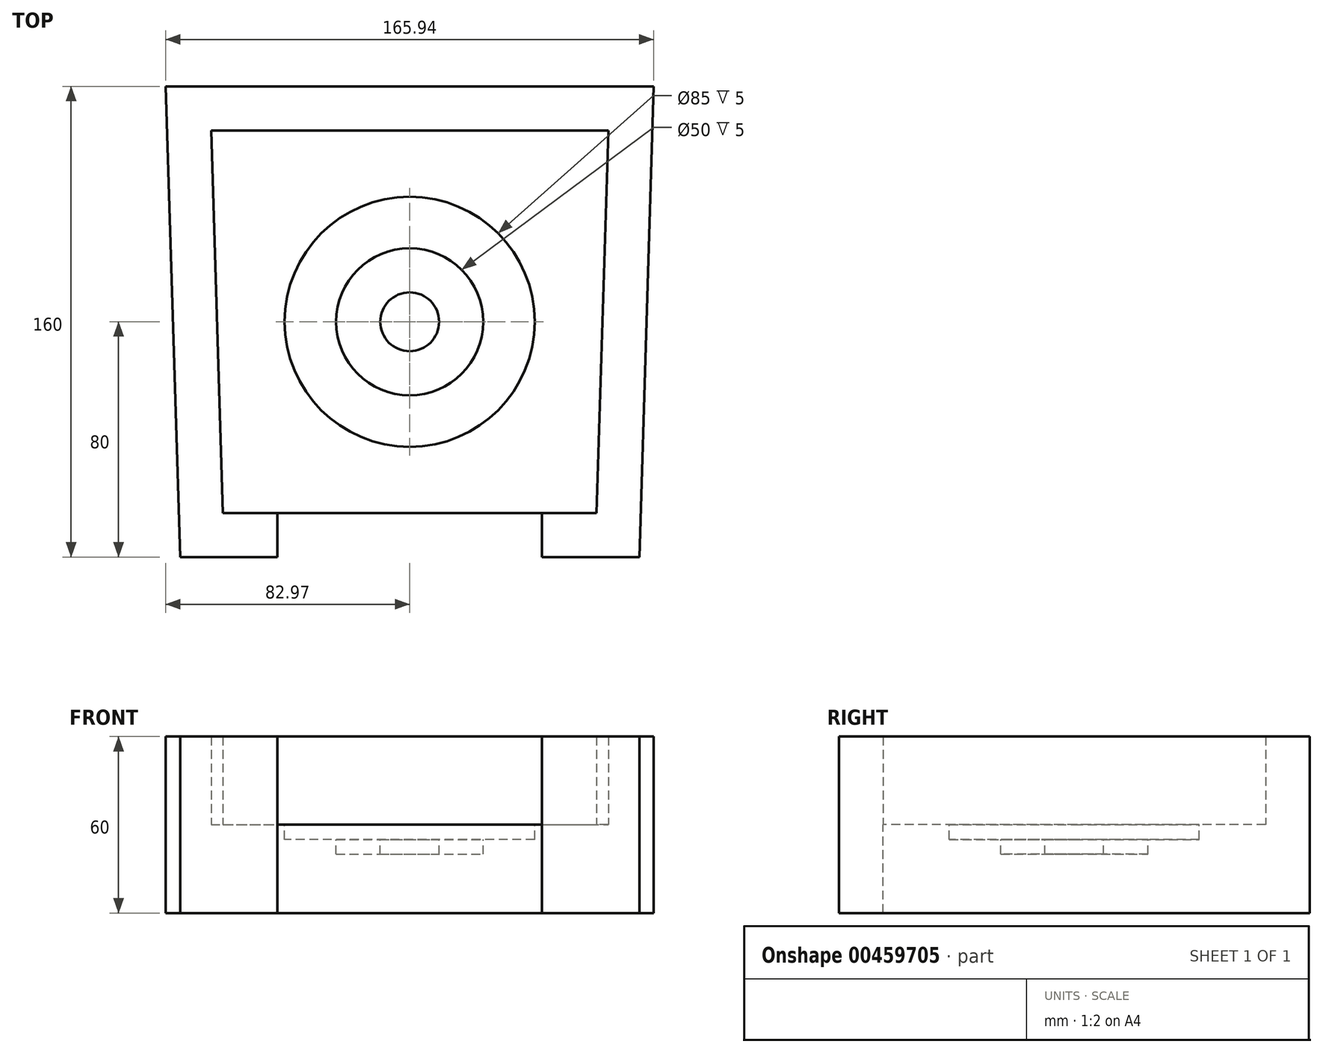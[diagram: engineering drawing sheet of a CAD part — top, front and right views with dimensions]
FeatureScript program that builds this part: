
annotation { "Feature Type Name" : "Feature", "Feature Type Description" : "" }
export const myFeature = defineFeature(function(context is Context, id is Id, definition is map)
    precondition{}
    {
        {
            var Q0;
            Q0=qCreatedBy(makeId("Top.planeOp"),FACE);
            var sketch = newSketch(context, id + "F0", { "sketchPlane" : qUnion([Q0])});
            skLineSegment(sketch, "E0", {"start": v(-67.5, 65) * mm, "end": v(-63.5, -65) * mm});
            skLineSegment(sketch, "E1", {"start": v(-63.5, -65) * mm, "end": v(63.5, -65) * mm});
            skLineSegment(sketch, "E2", {"start": v(-67.5, 65) * mm, "end": v(67.5, 65) * mm});
            skLineSegment(sketch, "E3", {"start": v(67.5, 65) * mm, "end": v(63.5, -65) * mm});
            skLineSegment(sketch, "E4", {"start": v(-82.97, 80) * mm, "end": v(-78.05, -80) * mm});
            skLineSegment(sketch, "E5", {"start": v(-78.05, -80) * mm, "end": v(78.05, -80) * mm});
            skLineSegment(sketch, "E6", {"start": v(-82.97, 80) * mm, "end": v(82.97, 80) * mm});
            skLineSegment(sketch, "E7", {"start": v(82.97, 80) * mm, "end": v(78.05, -80) * mm});
            skSolve(sketch);
        }
        {
            var Q0;
            Q0 = qSketchRegion(id + "F0", true);
            extrude(context, id + "F1", {"entities" : qUnion([Q0]), "depth" : 30 * mm});
        }
        {
            var Q0;
            Q0=makeQuery(id+"F1.opExtrude","SWEPT_FACE",FACE,{"disambiguationData":[OSD([sQuery(id+"F0.wireOp",EDGE,"E5")])]});
            var sketch = newSketch(context, id + "F2", { "sketchPlane" : qUnion([Q0])});
            skLineSegment(sketch, "E8.bottom", {"start": v(-45, 30) * mm, "end": v(45, 30) * mm});
            skLineSegment(sketch, "E8.top", {"start": v(-45, 0) * mm, "end": v(45, 0) * mm});
            skLineSegment(sketch, "E8.left", {"start": v(-45, 30) * mm, "end": v(-45, 0) * mm});
            skLineSegment(sketch, "E8.right", {"start": v(45, 30) * mm, "end": v(45, 0) * mm});
            skSolve(sketch);
        }
        {
            var Q0;
            Q0 = qSketchRegion(id + "F2", true);
            extrude(context, id + "F3", {"entities" : qUnion([Q0]), "operationType" : NewBodyOperationType.REMOVE, "endBound" : BoundingType.UP_TO_NEXT, "oppositeDirection" : true, "depth" : 35 * mm});
        }
        {
            var Q0;
            Q0=qCreatedBy(makeId("Top.planeOp"),FACE);
            var sketch = newSketch(context, id + "F4", { "sketchPlane" : qUnion([Q0])});
            skCircle(sketch, "E9", {"center": v(0, 0) * mm, "radius": 42.5 * mm});
            skLineSegment(sketch, "E10.bottom", {"start": v(-82.97, 80) * mm, "end": v(82.97, 80) * mm});
            skLineSegment(sketch, "E10.top", {"start": v(-45, -65) * mm, "end": v(45, -65) * mm});
            skLineSegment(sketch, "E11", {"start": v(45, -65) * mm, "end": v(45, -80) * mm});
            skLineSegment(sketch, "E12", {"start": v(-45, -65) * mm, "end": v(-45, -80) * mm});
            skLineSegment(sketch, "E13", {"start": v(-45, -80) * mm, "end": v(-78.05, -80) * mm});
            skLineSegment(sketch, "E14", {"start": v(-78.05, -80) * mm, "end": v(-82.97, 80) * mm});
            skLineSegment(sketch, "E15", {"start": v(45, -80) * mm, "end": v(78.05, -80) * mm});
            skLineSegment(sketch, "E16", {"start": v(78.05, -80) * mm, "end": v(82.97, 80) * mm});
            skSolve(sketch);
        }
        {
            var Q0;
            Q0 = qSketchRegion(id + "F4", true);
            extrude(context, id + "F5", {"entities" : qUnion([Q0]), "operationType" : NewBodyOperationType.ADD, "oppositeDirection" : true, "depth" : 5 * mm});
        }
        {
            var Q0;
            Q0=makeQuery(id+"F5.opExtrude","CAP_FACE",FACE,{"disambiguationData":[OSD([sQuery(id+"F4.wireOp",EDGE,"E9"),sQuery(id+"F4.wireOp",EDGE,"E10.bottom"),sQuery(id+"F4.wireOp",EDGE,"E10.top"),sQuery(id+"F4.wireOp",EDGE,"E11"),sQuery(id+"F4.wireOp",EDGE,"E12"),sQuery(id+"F4.wireOp",EDGE,"E13"),sQuery(id+"F4.wireOp",EDGE,"E14"),sQuery(id+"F4.wireOp",EDGE,"E15"),sQuery(id+"F4.wireOp",EDGE,"E16")])],"isStart":false});
            var sketch = newSketch(context, id + "F6", { "sketchPlane" : qUnion([Q0])});
            skCircle(sketch, "E17", {"center": v(0, 0) * mm, "radius": 10 * mm});
            skSolve(sketch);
        }
        {
            var Q0;
            Q0 = qSketchRegion(id + "F6", true);
            extrude(context, id + "F7", {"entities" : qUnion([Q0]), "depth" : 5 * mm});
        }
        {
            var Q0;
            Q0=makeQuery(id+"F5.opExtrude","CAP_FACE",FACE,{"disambiguationData":[OSD([sQuery(id+"F4.wireOp",EDGE,"E9"),sQuery(id+"F4.wireOp",EDGE,"E10.bottom"),sQuery(id+"F4.wireOp",EDGE,"E10.top"),sQuery(id+"F4.wireOp",EDGE,"E11"),sQuery(id+"F4.wireOp",EDGE,"E12"),sQuery(id+"F4.wireOp",EDGE,"E13"),sQuery(id+"F4.wireOp",EDGE,"E14"),sQuery(id+"F4.wireOp",EDGE,"E15"),sQuery(id+"F4.wireOp",EDGE,"E16")])],"isStart":false});
            var sketch = newSketch(context, id + "F8", { "sketchPlane" : qUnion([Q0])});
            skCircle(sketch, "E18", {"center": v(0, 0) * mm, "radius": 25 * mm});
            skLineSegment(sketch, "E19", {"start": v(-78.05, 80) * mm, "end": v(-82.97, -80) * mm});
            skLineSegment(sketch, "E20", {"start": v(-82.97, -80) * mm, "end": v(82.97, -80) * mm});
            skLineSegment(sketch, "E21", {"start": v(82.97, -80) * mm, "end": v(78.05, 80) * mm});
            skLineSegment(sketch, "E22", {"start": v(78.05, 80) * mm, "end": v(45, 80) * mm});
            skLineSegment(sketch, "E23", {"start": v(45, 80) * mm, "end": v(45, 65) * mm});
            skLineSegment(sketch, "E24", {"start": v(45, 65) * mm, "end": v(-45, 65) * mm});
            skLineSegment(sketch, "E25", {"start": v(-45, 65) * mm, "end": v(-45, 80) * mm});
            skLineSegment(sketch, "E26", {"start": v(-45, 80) * mm, "end": v(-78.05, 80) * mm});
            skSolve(sketch);
        }
        {
            var Q0;
            Q0 = qSketchRegion(id + "F8", true);
            extrude(context, id + "F9", {"entities" : qUnion([Q0]), "operationType" : NewBodyOperationType.ADD, "depth" : 5 * mm});
        }
        {
            var Q0;
            Q0=makeQuery(id+"F9.opExtrude","CAP_FACE",FACE,{"disambiguationData":[OSD([sQuery(id+"F8.wireOp",EDGE,"E18"),sQuery(id+"F8.wireOp",EDGE,"E19"),sQuery(id+"F8.wireOp",EDGE,"E20"),sQuery(id+"F8.wireOp",EDGE,"E21"),sQuery(id+"F8.wireOp",EDGE,"E22"),sQuery(id+"F8.wireOp",EDGE,"E23"),sQuery(id+"F8.wireOp",EDGE,"E24"),sQuery(id+"F8.wireOp",EDGE,"E25"),sQuery(id+"F8.wireOp",EDGE,"E26")])],"isStart":false});
            var sketch = newSketch(context, id + "F10", { "sketchPlane" : qUnion([Q0])});
            skLineSegment(sketch, "E27", {"start": v(-82.97, -80) * mm, "end": v(82.97, -80) * mm});
            skLineSegment(sketch, "E28", {"start": v(82.97, -80) * mm, "end": v(78.05, 80) * mm});
            skLineSegment(sketch, "E29", {"start": v(78.05, 80) * mm, "end": v(45, 80) * mm});
            skLineSegment(sketch, "E30", {"start": v(45, 80) * mm, "end": v(45, 65) * mm});
            skLineSegment(sketch, "E31", {"start": v(45, 65) * mm, "end": v(-45, 65) * mm});
            skLineSegment(sketch, "E32", {"start": v(-45, 65) * mm, "end": v(-45, 80) * mm});
            skLineSegment(sketch, "E33", {"start": v(-45, 80) * mm, "end": v(-78.05, 80) * mm});
            skLineSegment(sketch, "E34", {"start": v(-78.05, 80) * mm, "end": v(-82.97, -80) * mm});
            skSolve(sketch);
        }
        {
            var Q0;
            Q0 = qSketchRegion(id + "F10", true);
            extrude(context, id + "F11", {"entities" : qUnion([Q0]), "operationType" : NewBodyOperationType.ADD, "depth" : 20 * mm});
        }
    });
